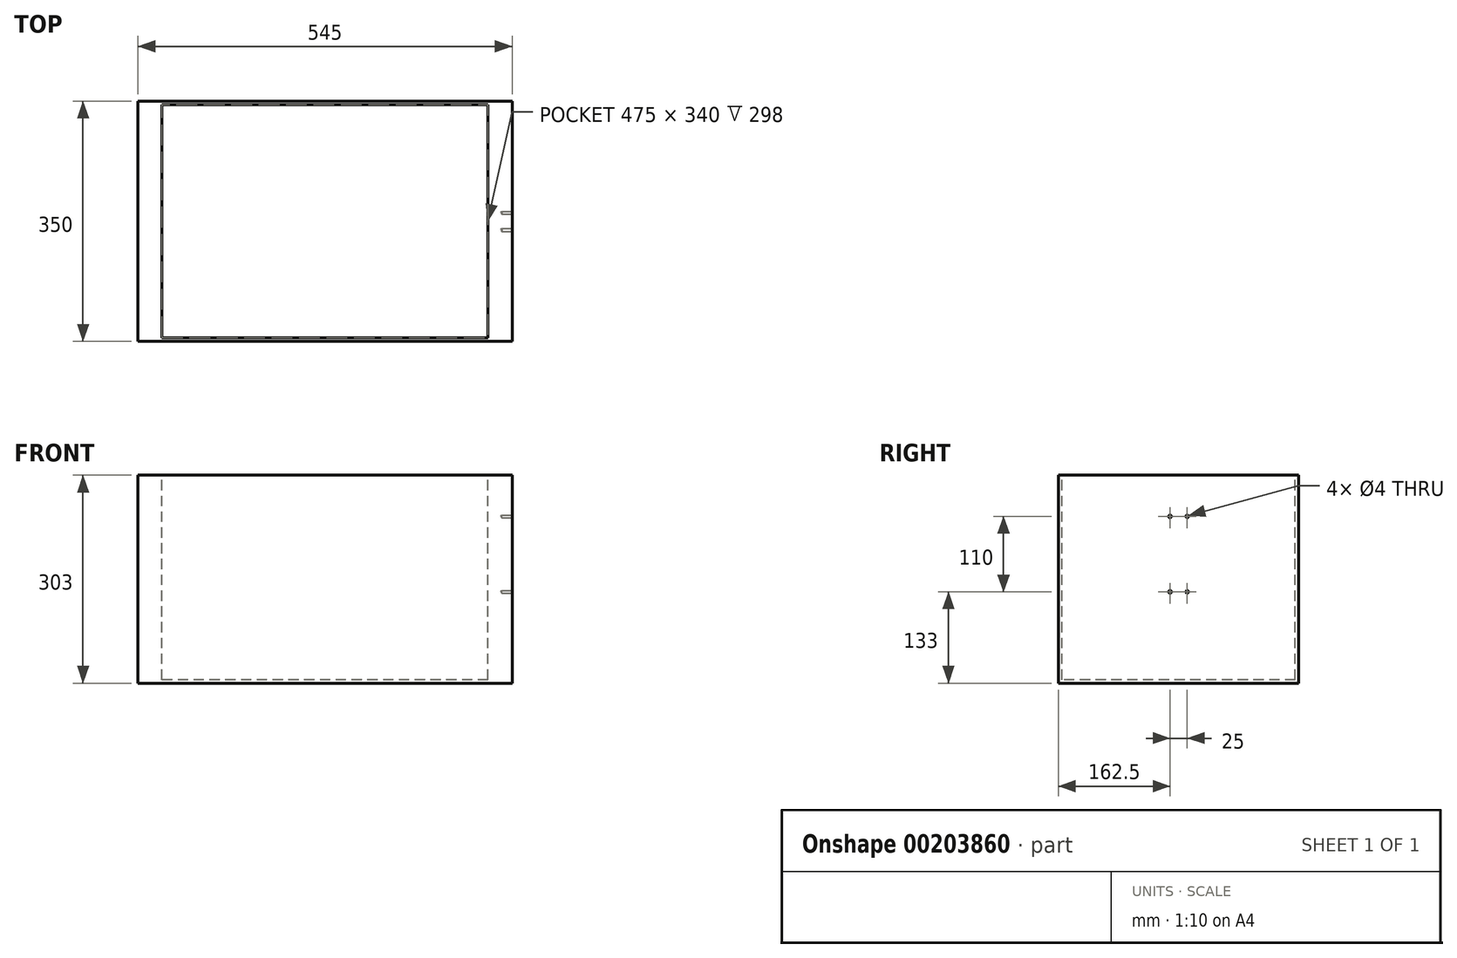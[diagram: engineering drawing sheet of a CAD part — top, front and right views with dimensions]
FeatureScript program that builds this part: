
annotation { "Feature Type Name" : "Feature", "Feature Type Description" : "" }
export const myFeature = defineFeature(function(context is Context, id is Id, definition is map)
    precondition{}
    {
        {
            var Q0;
            Q0=qCreatedBy(makeId("Top.planeOp"),FACE);
            var sketch = newSketch(context, id + "F0", { "sketchPlane" : qUnion([Q0])});
            skLineSegment(sketch, "E0.bottom", {"start": v(272.5, 175) * mm, "end": v(-272.5, 175) * mm});
            skLineSegment(sketch, "E0.top", {"start": v(272.5, -175) * mm, "end": v(-272.5, -175) * mm});
            skLineSegment(sketch, "E0.left", {"start": v(272.5, 175) * mm, "end": v(272.5, -175) * mm});
            skLineSegment(sketch, "E0.right", {"start": v(-272.5, 175) * mm, "end": v(-272.5, -175) * mm});
            skPoint(sketch, "E0.middle", {"position": v(0, 0) * mm});
            skLineSegment(sketch, "E1.bottom", {"start": v(237.5, 170) * mm, "end": v(-237.5, 170) * mm});
            skLineSegment(sketch, "E1.top", {"start": v(237.5, -170) * mm, "end": v(-237.5, -170) * mm});
            skLineSegment(sketch, "E1.left", {"start": v(237.5, 170) * mm, "end": v(237.5, -170) * mm});
            skLineSegment(sketch, "E1.right", {"start": v(-237.5, 170) * mm, "end": v(-237.5, -170) * mm});
            skSolve(sketch);
        }
        {
            var Q0;
            Q0=makeQuery(id+"F0.imprint","IMPRINT",FACE,{"disambiguationData":[TD([[makeQuery(id+"F0.imprint","IMPRINT",EDGE,{"derivedFrom":sQuery(id+"F0.wireOp",EDGE,"E0.bottom")}),1.0]])]});
            extrude(context, id + "F1", {"entities" : qUnion([Q0]), "endBound" : BoundingType.SYMMETRIC, "oppositeDirection" : true, "depth" : 298 * mm});
        }
        {
            var Q0;
            Q0=makeQuery(id+"F1.opExtrude","SWEPT_FACE",FACE,{"disambiguationData":[OSD([sQuery(id+"F0.wireOp",EDGE,"E0.left")])]});
            var sketch = newSketch(context, id + "F2", { "sketchPlane" : qUnion([Q0])});
            skPoint(sketch, "E2", {"position": v(-12.5, -21) * mm});
            skPoint(sketch, "E3", {"position": v(-12.5, 89) * mm});
            skPoint(sketch, "E4.MirrorP", {"position": v(12.5, 89) * mm});
            skPoint(sketch, "E5.MirrorP", {"position": v(12.5, -21) * mm});
            skSolve(sketch);
        }
        {
            var Q0;
            Q0=makeQuery(id+"F1.opExtrude","CAP_FACE",FACE,{"disambiguationData":[OSD([sQuery(id+"F0.wireOp",EDGE,"E0.bottom"),sQuery(id+"F0.wireOp",EDGE,"E0.top"),sQuery(id+"F0.wireOp",EDGE,"E0.left"),sQuery(id+"F0.wireOp",EDGE,"E0.right"),sQuery(id+"F0.wireOp",EDGE,"E1.bottom"),sQuery(id+"F0.wireOp",EDGE,"E1.top"),sQuery(id+"F0.wireOp",EDGE,"E1.left"),sQuery(id+"F0.wireOp",EDGE,"E1.right")])],"isStart":false});
            var sketch = newSketch(context, id + "F3", { "sketchPlane" : qUnion([Q0])});
            skLineSegment(sketch, "E6.bottom", {"start": v(272.5, -175) * mm, "end": v(-272.5, -175) * mm});
            skLineSegment(sketch, "E6.top", {"start": v(272.5, 175) * mm, "end": v(-272.5, 175) * mm});
            skLineSegment(sketch, "E6.left", {"start": v(272.5, 175) * mm, "end": v(272.5, -175) * mm});
            skLineSegment(sketch, "E6.right", {"start": v(-272.5, 175) * mm, "end": v(-272.5, -175) * mm});
            skPoint(sketch, "E6.middle", {"position": v(0, 0) * mm});
            skSolve(sketch);
        }
        {
            var Q0;
            Q0 = qSketchRegion(id + "F3", true);
            extrude(context, id + "F4", {"entities" : qUnion([Q0]), "operationType" : NewBodyOperationType.ADD, "depth" : 5 * mm});
        }
        {
            var Q0;
            Q0=sQuery(id+"F2.wireOp",VERTEX,"E3");
            var Q1;
            Q1=sQuery(id+"F2.wireOp",VERTEX,"E4.MirrorP");
            var Q2;
            Q2=sQuery(id+"F2.wireOp",VERTEX,"E2");
            var Q3;
            Q3=sQuery(id+"F2.wireOp",VERTEX,"E5.MirrorP");
            var Q4;
            Q4=makeQuery(id+"F1.opExtrude","SWEPT_BODY",BODY,{"disambiguationData":[OSD([sQuery(id+"F0.wireOp",EDGE,"E0.bottom"),sQuery(id+"F0.wireOp",EDGE,"E0.top"),sQuery(id+"F0.wireOp",EDGE,"E0.left"),sQuery(id+"F0.wireOp",EDGE,"E0.right"),sQuery(id+"F0.wireOp",EDGE,"E1.bottom"),sQuery(id+"F0.wireOp",EDGE,"E1.top"),sQuery(id+"F0.wireOp",EDGE,"E1.left"),sQuery(id+"F0.wireOp",EDGE,"E1.right")])]});
            hole(context, id + "F5", {"style" : HoleStyle.SIMPLE, "endStyle" : HoleEndStyle.BLIND, "holeDiameter" : 4 * mm, "holeDepth" : 15 * mm, "locations" : qUnion([Q0, Q1, Q2, Q3]), "scope" : qUnion([Q4])});
        }
    });
